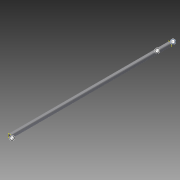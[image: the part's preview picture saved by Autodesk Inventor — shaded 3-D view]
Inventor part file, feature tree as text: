
AUTODESK INVENTOR PART (.ipt)
format: ipt  version: 2015 (Build 190159000, 159)  size: 137,728 bytes
history: native  units: in
note: dims shown in document units (in); Inventor stores cm internally (conversion verified against a paired STEP export)
features: other x4, extrude x1, imported_body x1, sketch x1
ambient origin geometry x8: Origin, YZ Plane, XZ Plane, XY Plane, X Axis, Y Axis, Z Axis, Center Point
bodies: Body1 (feature_tree)
feature tree (7):
  other  "Cut-Revolve3"
  other  "Shaft HS 12.0 inch"
  extrude  "Extrusion1"  TaperAngle=0.0deg  [1 undecoded]
  other  "Front Plane"
  imported_body  "Base1"
  other  "back plane"
  sketch  "Sketch1"  dims[d0=0.0in d2=0.0in d3=-12.0in d4=0.0in d5=0.0in d6=0.0in]
note: 1 required parameter value undecoded (feature->parameter linkage not recoverable at this tier; creation-order binding heuristic only, values carry confidence <= 0.55)
